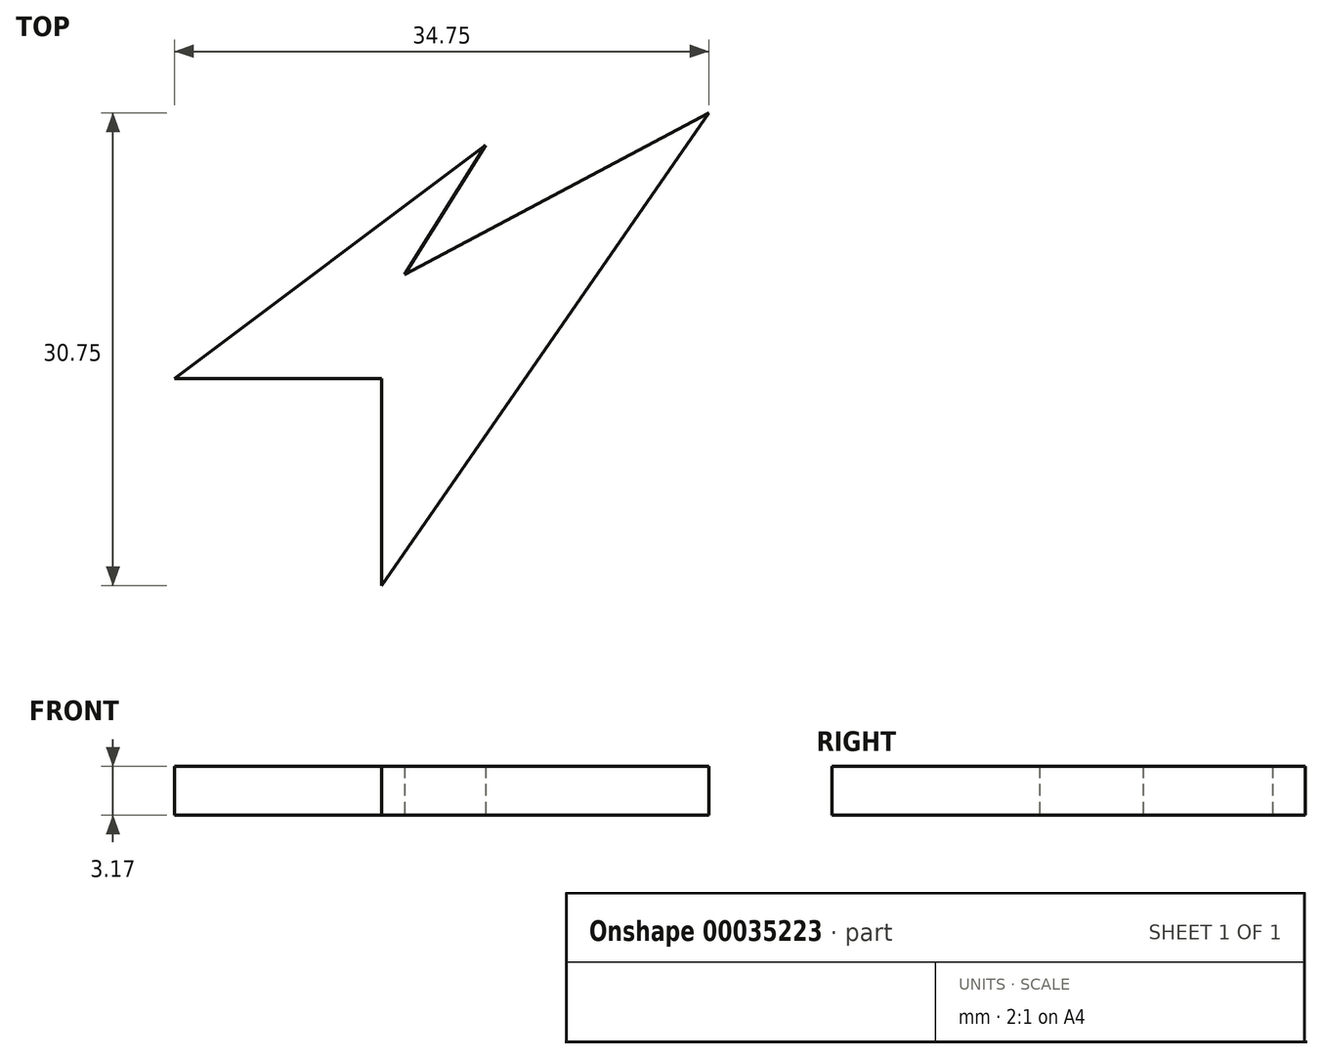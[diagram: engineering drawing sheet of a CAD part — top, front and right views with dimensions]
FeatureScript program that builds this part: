
annotation { "Feature Type Name" : "Feature", "Feature Type Description" : "" }
export const myFeature = defineFeature(function(context is Context, id is Id, definition is map)
    precondition{}
    {
        {
            var Q0;
            Q0=qCreatedBy(makeId("Top.planeOp"),FACE);
            var sketch = newSketch(context, id + "F0", { "sketchPlane" : qUnion([Q0])});
            skLineSegment(sketch, "E0", {"start": v(4.07, 10.88) * mm, "end": v(-16.15, -4.28) * mm});
            skLineSegment(sketch, "E1", {"start": v(-1.2, 2.46) * mm, "end": v(4.07, 10.88) * mm});
            skLineSegment(sketch, "E2", {"start": v(18.6, 12.99) * mm, "end": v(-1.2, 2.46) * mm});
            skLineSegment(sketch, "E3", {"start": v(-2.67, -17.76) * mm, "end": v(18.6, 12.99) * mm});
            skLineSegment(sketch, "E4", {"start": v(-16.15, -4.28) * mm, "end": v(-2.67, -4.28) * mm});
            skLineSegment(sketch, "E5", {"start": v(-2.67, -4.28) * mm, "end": v(-2.67, -17.76) * mm});
            skSolve(sketch);
        }
        {
            var Q0;
            Q0=makeQuery(id+"F0.imprint","IMPRINT",FACE,{"disambiguationData":[TD([[makeQuery(id+"F0.imprint","IMPRINT",EDGE,{"derivedFrom":sQuery(id+"F0.wireOp",EDGE,"E0")}),1.0]])]});
            extrude(context, id + "F1", {"entities" : qUnion([Q0]), "depth" : 3.17 * mm});
        }
    });
